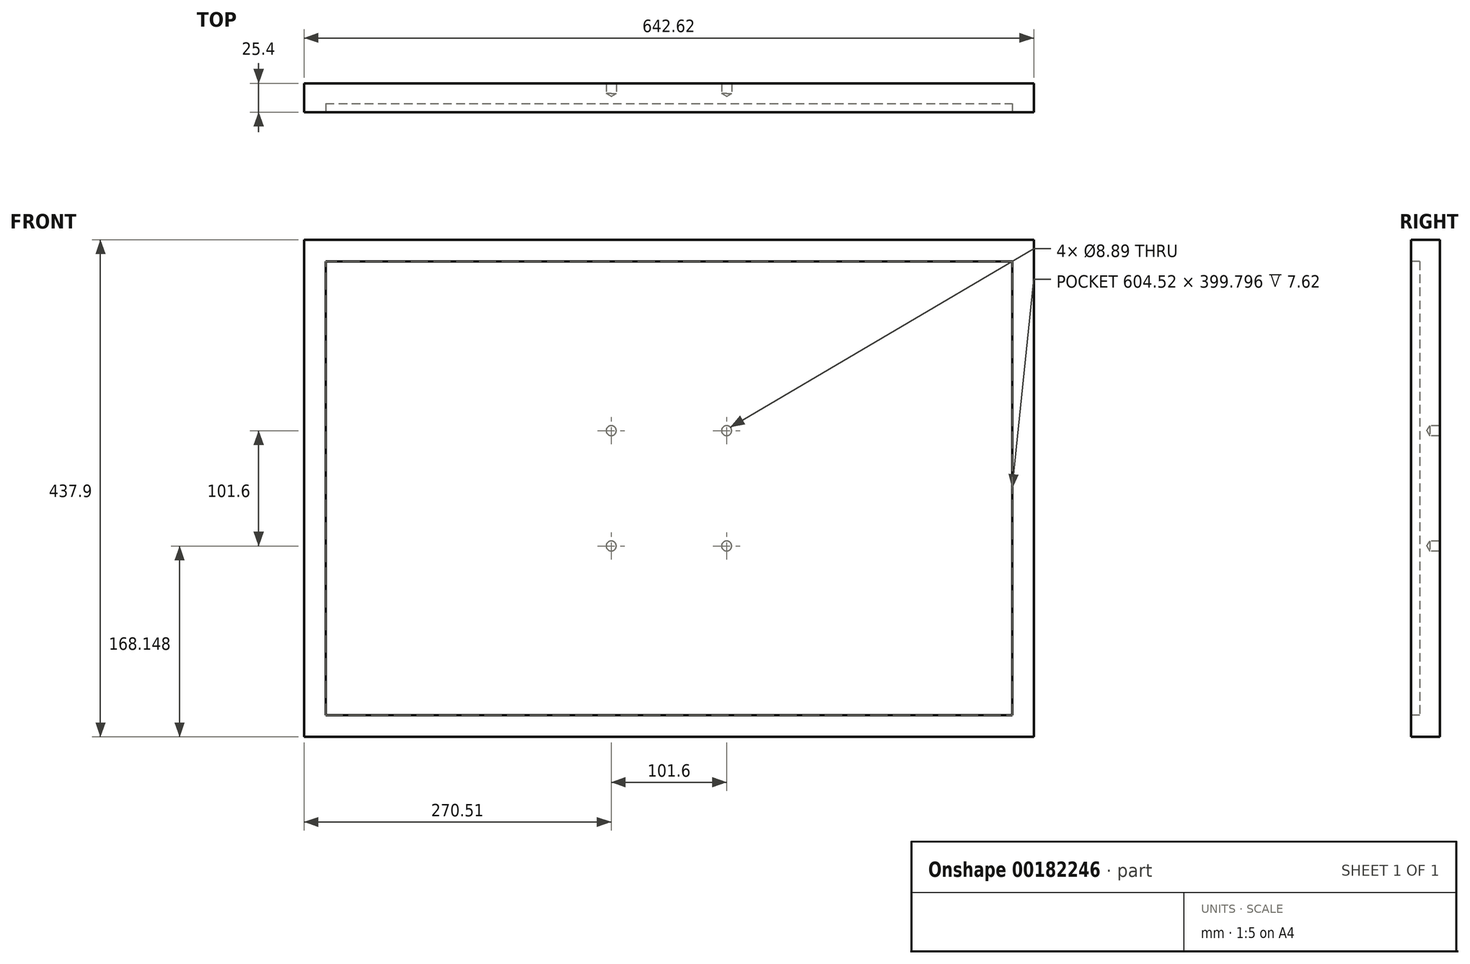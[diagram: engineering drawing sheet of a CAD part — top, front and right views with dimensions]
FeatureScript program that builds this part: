
annotation { "Feature Type Name" : "Feature", "Feature Type Description" : "" }
export const myFeature = defineFeature(function(context is Context, id is Id, definition is map)
    precondition{}
    {
        {
            var Q0;
            Q0=qCreatedBy(makeId("Front.planeOp"),FACE);
            var sketch = newSketch(context, id + "F0", { "sketchPlane" : qUnion([Q0])});
            skLineSegment(sketch, "E0.bottom", {"start": v(0, 0) * mm, "end": v(642.62, 0) * mm});
            skLineSegment(sketch, "E0.top", {"start": v(0, 437.9) * mm, "end": v(642.62, 437.9) * mm});
            skLineSegment(sketch, "E0.left", {"start": v(0, 0) * mm, "end": v(0, 437.9) * mm});
            skLineSegment(sketch, "E0.right", {"start": v(642.62, 0) * mm, "end": v(642.62, 437.9) * mm});
            skSolve(sketch);
        }
        {
            var Q0;
            Q0=makeQuery(id+"F0.imprint","IMPRINT",FACE,{"disambiguationData":[TD([[makeQuery(id+"F0.imprint","IMPRINT",EDGE,{"derivedFrom":sQuery(id+"F0.wireOp",EDGE,"E0.bottom")}),1.0]])]});
            extrude(context, id + "F1", {"entities" : qUnion([Q0]), "depth" : 25.4 * mm});
        }
        {
            var Q0;
            Q0=makeQuery(id+"F1.opExtrude","CAP_FACE",FACE,{"disambiguationData":[OSD([sQuery(id+"F0.wireOp",EDGE,"E0.bottom"),sQuery(id+"F0.wireOp",EDGE,"E0.top"),sQuery(id+"F0.wireOp",EDGE,"E0.left"),sQuery(id+"F0.wireOp",EDGE,"E0.right")])],"isStart":true});
            var sketch = newSketch(context, id + "F2", { "sketchPlane" : qUnion([Q0])});
            skLineSegment(sketch, "E1", {"start": v(-596.52, 269.75) * mm, "end": v(-137.43, 269.75) * mm, "construction": true});
            skLineSegment(sketch, "E2", {"start": v(-600.31, 168.15) * mm, "end": v(-136.29, 168.15) * mm, "construction": true});
            skLineSegment(sketch, "E3", {"start": v(-372.11, 575.74) * mm, "end": v(-372.1, -29.26) * mm, "construction": true});
            skLineSegment(sketch, "E4", {"start": v(-270.51, 575.1) * mm, "end": v(-270.5, -39.45) * mm, "construction": true});
            skPoint(sketch, "E5", {"position": v(-372.11, 269.75) * mm});
            skPoint(sketch, "E6", {"position": v(-270.51, 269.75) * mm});
            skPoint(sketch, "E7", {"position": v(-270.51, 168.15) * mm});
            skPoint(sketch, "E8", {"position": v(-372.11, 168.15) * mm});
            skSolve(sketch);
        }
        {
            var Q0;
            Q0=sQuery(id+"F2.wireOp",VERTEX,"E5");
            var Q1;
            Q1=sQuery(id+"F2.wireOp",VERTEX,"E6");
            var Q2;
            Q2=sQuery(id+"F2.wireOp",VERTEX,"E7");
            var Q3;
            Q3=sQuery(id+"F2.wireOp",VERTEX,"E8");
            var Q4;
            Q4=makeQuery(id+"F1.opExtrude","SWEPT_BODY",BODY,{"disambiguationData":[OSD([sQuery(id+"F0.wireOp",EDGE,"E0.bottom"),sQuery(id+"F0.wireOp",EDGE,"E0.top"),sQuery(id+"F0.wireOp",EDGE,"E0.left"),sQuery(id+"F0.wireOp",EDGE,"E0.right")])]});
            hole(context, id + "F3", {"style" : HoleStyle.SIMPLE, "holeDiameter" : 8.9 * mm, "endStyle" : HoleEndStyle.BLIND, "holeDepth" : 8.9 * mm, "locations" : qUnion([Q0, Q1, Q2, Q3]), "scope" : qUnion([Q4])});
        }
        {
            var Q0;
            Q0=makeQuery(id+"F1.opExtrude","CAP_FACE",FACE,{"disambiguationData":[OSD([sQuery(id+"F0.wireOp",EDGE,"E0.bottom"),sQuery(id+"F0.wireOp",EDGE,"E0.top"),sQuery(id+"F0.wireOp",EDGE,"E0.left"),sQuery(id+"F0.wireOp",EDGE,"E0.right")])],"isStart":false});
            var sketch = newSketch(context, id + "F4", { "sketchPlane" : qUnion([Q0])});
            skLineSegment(sketch, "E9.bottom", {"start": v(19.05, 418.85) * mm, "end": v(623.57, 418.85) * mm});
            skLineSegment(sketch, "E9.top", {"start": v(19.05, 19.05) * mm, "end": v(623.57, 19.05) * mm});
            skLineSegment(sketch, "E9.left", {"start": v(19.05, 418.85) * mm, "end": v(19.05, 19.05) * mm});
            skLineSegment(sketch, "E9.right", {"start": v(623.57, 418.85) * mm, "end": v(623.57, 19.05) * mm});
            skSolve(sketch);
        }
        {
            var Q0;
            Q0=qSketchRegion(id+"F4",true);
            extrude(context, id + "F5", {"entities" : qUnion([Q0]), "operationType" : NewBodyOperationType.REMOVE, "oppositeDirection" : true, "depth" : 7.62 * mm});
        }
    });
